# Revit family: Sink_Quartz_Undermount-Elkay-ELXULB4522WFX0_CA0_CH0_CN0_RT0_SN0_SM0
name_source: partatom
category: Plumbing Fixtures
units: mm (PartAtom-declared; Revit-internal decimal feet)

## family parameters
Cut with Voids When Loaded = No
Host = Face
Maintain Annotation Orientation = No
OmniClass Number = 23.45.05.14.14
OmniClass Title = Sinks/Lavatories
Part Type = Normal
Room Calculation Point = No
Round Connector Dimension = Use Diameter
Shared = No

## types (7) — shared parameters
Approx. Shipping Weight (lbs) = 64
Assembly Code = D2010400
Bowl 1  Dimensions = 16 9/16 inch x 17 1/16 inch x  9 1/2 inch
Bowl 2  Dimensions = 24 1/8 inch x 17 1/16 inch x  9 5/8 inch
Cutting Length = 42.875 "
Cutting Width = 17.25 "
Default Elevation = 48 "
Description = Quartz Luxe® 45 inch x 19 inch x  9 inch 60/40 Undermount Workstation Sink Kit with Perfect Drain and Aqua Divide
Drain Location = Center
Installation Type = UnderMount
Length of sink = 45 "
Manufacturer = Elkay Manufacturer Company
Manufacturer Brand = Elkay (by Zurn Elkay Water Solutions)
Number of Bowls = 2
Outlet Connection Size (inch) = 1.5 "
Product Documentation Link = https://www.elkayfiles.com
Product Installation Sheet URL = https://www.elkayfiles.com
Product Page URL = https://www.elkay.com
Product Weight (lbs) = 48
Product data URL = https://bimobject.com
Repair Parts URL = https://www.elkayfiles.com
Sink Depth = 11 "
Sink Dimensions = 45 inch x 19 inch x  11 inch
Type Image = <None>
URL = https://www.elkay.com
Waste Connection = No
Width of sink = 19 "

## per-type parameters (varying)
| type | Main Material | Model |
| ELXULB4522WFX0 (Quartz Luxe Undermount Workstation Sink Kit with Perfect Drain and Aqua Divide) | Finish-Elkay-Arctic fox | ELXULB4522WFX0 |
| ELXULB4522WCA0 (Quartz Luxe Undermount Workstation Sink Kit with Perfect Drain and Aqua Divide) | Finish-Elkay-Caviar | ELXULB4522WCA0 |
| ELXULB4522WCH0 (Quartz Luxe Undermount Workstation Sink Kit with Perfect Drain and Aqua Divide) | Finish-Elkay-Charcoal | ELXULB4522WCH0 |
| ELXULB4522WCN0 (Quartz Luxe Undermount Workstation Sink Kit with Perfect Drain and Aqua Divide) | Finish-Elkay-Chestnut | ELXULB4522WCN0 |
| ELXULB4522WRT0 (Quartz Luxe Undermount Workstation Sink Kit with Perfect Drain and Aqua Divide) | Finish-Elkay-Ricotta | ELXULB4522WRT0 |
| ELXULB4522WSN0 (Quartz Luxe Undermount Workstation Sink Kit with Perfect Drain and Aqua Divide) | Finish-Elkay-Sandstone | ELXULB4522WSN0 |
| ELXULB4522WSM0 (Quartz Luxe Undermount Workstation Sink Kit with Perfect Drain and Aqua Divide) | Finish-Elkay-Silvermist | ELXULB4522WSM0 |

## geometry (parser evidence)
native form markers: Sweep x5
no freeform markers — native parametric forms only
